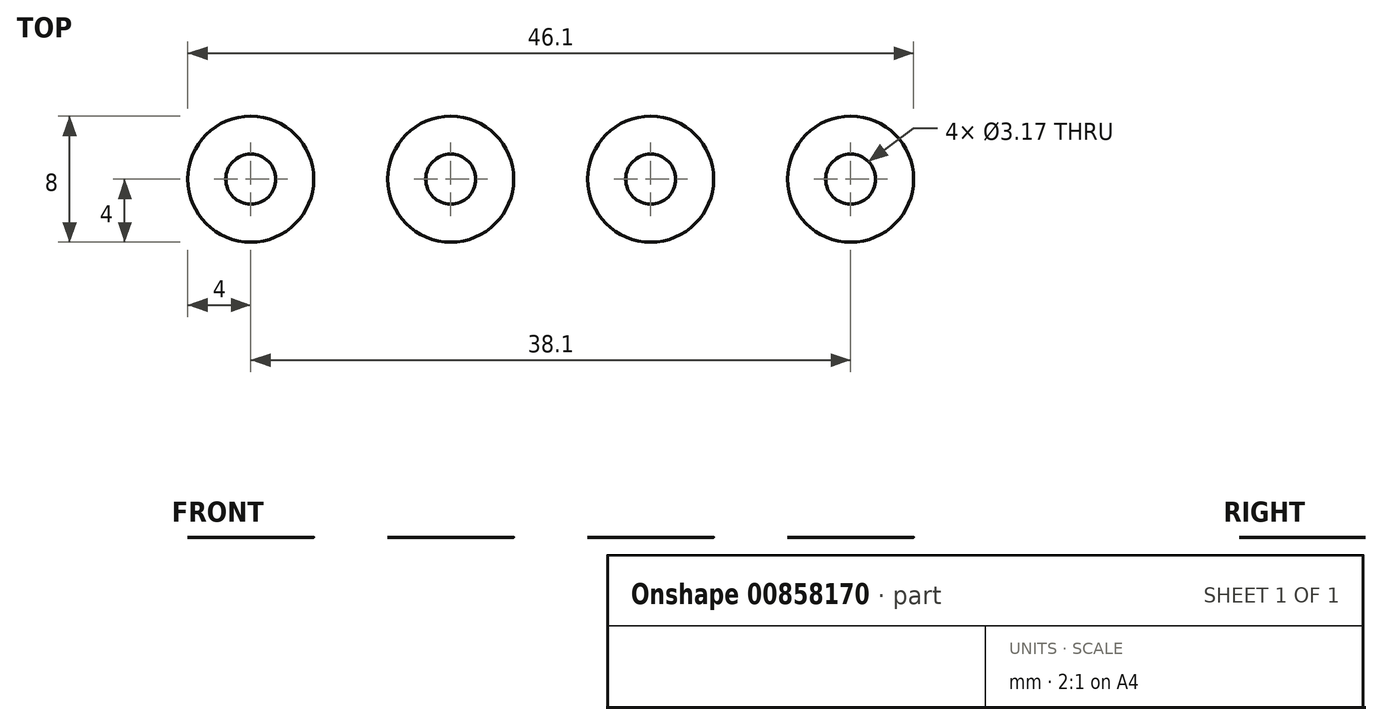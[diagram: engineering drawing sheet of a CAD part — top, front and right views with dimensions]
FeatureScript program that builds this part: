
annotation { "Feature Type Name" : "Feature", "Feature Type Description" : "" }
export const myFeature = defineFeature(function(context is Context, id is Id, definition is map)
    precondition{}
    {
        {
            var Q0;
            Q0=qCreatedBy(makeId("Top.planeOp"),FACE);
            var sketch = newSketch(context, id + "F0", { "sketchPlane" : qUnion([Q0])});
            skCircle(sketch, "E0", {"center": v(0, 0) * mm, "radius": 4 * mm});
            skCircle(sketch, "E1", {"center": v(0, 0) * mm, "radius": 1.59 * mm});
            skSolve(sketch);
        }
        {
            var Q0;
            Q0=makeQuery(id+"F0.imprint","IMPRINT",FACE,{"disambiguationData":[TD([[makeQuery(id+"F0.imprint","IMPRINT",EDGE,{"derivedFrom":sQuery(id+"F0.wireOp",EDGE,"E0")}),1.0]])]});
            extrude(context, id + "F1", {"entities" : qUnion([Q0]), "depth" : 1 / 203.2 * mm, "offsetDistance" : 25.4 * mm});
        }
        {
            var Q0;
            Q0=makeQuery(id+"F1.opExtrude","SWEPT_BODY",BODY,{"disambiguationData":[OSD([sQuery(id+"F0.wireOp",EDGE,"E0"),sQuery(id+"F0.wireOp",EDGE,"E1")])]});
            transform(context, id + "F2", {"entities" : qUnion([Q0]), "transformType" : TransformType.TRANSLATION_3D, "dx" : 25.4 * mm, "dy" : 0 * mm, "dz" : 0 * mm, "makeCopy" : true});
        }
        {
            var Q0;
            Q0=makeQuery(id+"F2.opPattern","COPY",BODY,{"derivedFrom":makeQuery(id+"F1.opExtrude","SWEPT_BODY",BODY,{"disambiguationData":[OSD([sQuery(id+"F0.wireOp",EDGE,"E0"),sQuery(id+"F0.wireOp",EDGE,"E1")])]}),"instanceName":"1"});
            transform(context, id + "F3", {"entities" : qUnion([Q0]), "transformType" : TransformType.TRANSLATION_3D, "dx" : -12.7 * mm, "dy" : 0 * mm, "dz" : 0 * mm, "makeCopy" : true});
        }
        {
            var Q0;
            Q0=makeQuery(id+"F1.opExtrude","SWEPT_BODY",BODY,{"disambiguationData":[OSD([sQuery(id+"F0.wireOp",EDGE,"E0"),sQuery(id+"F0.wireOp",EDGE,"E1")])]});
            transform(context, id + "F4", {"entities" : qUnion([Q0]), "transformType" : TransformType.TRANSLATION_3D, "dx" : -12.7 * mm, "dy" : 0 * mm, "dz" : 0 * mm, "makeCopy" : true});
        }
    });
